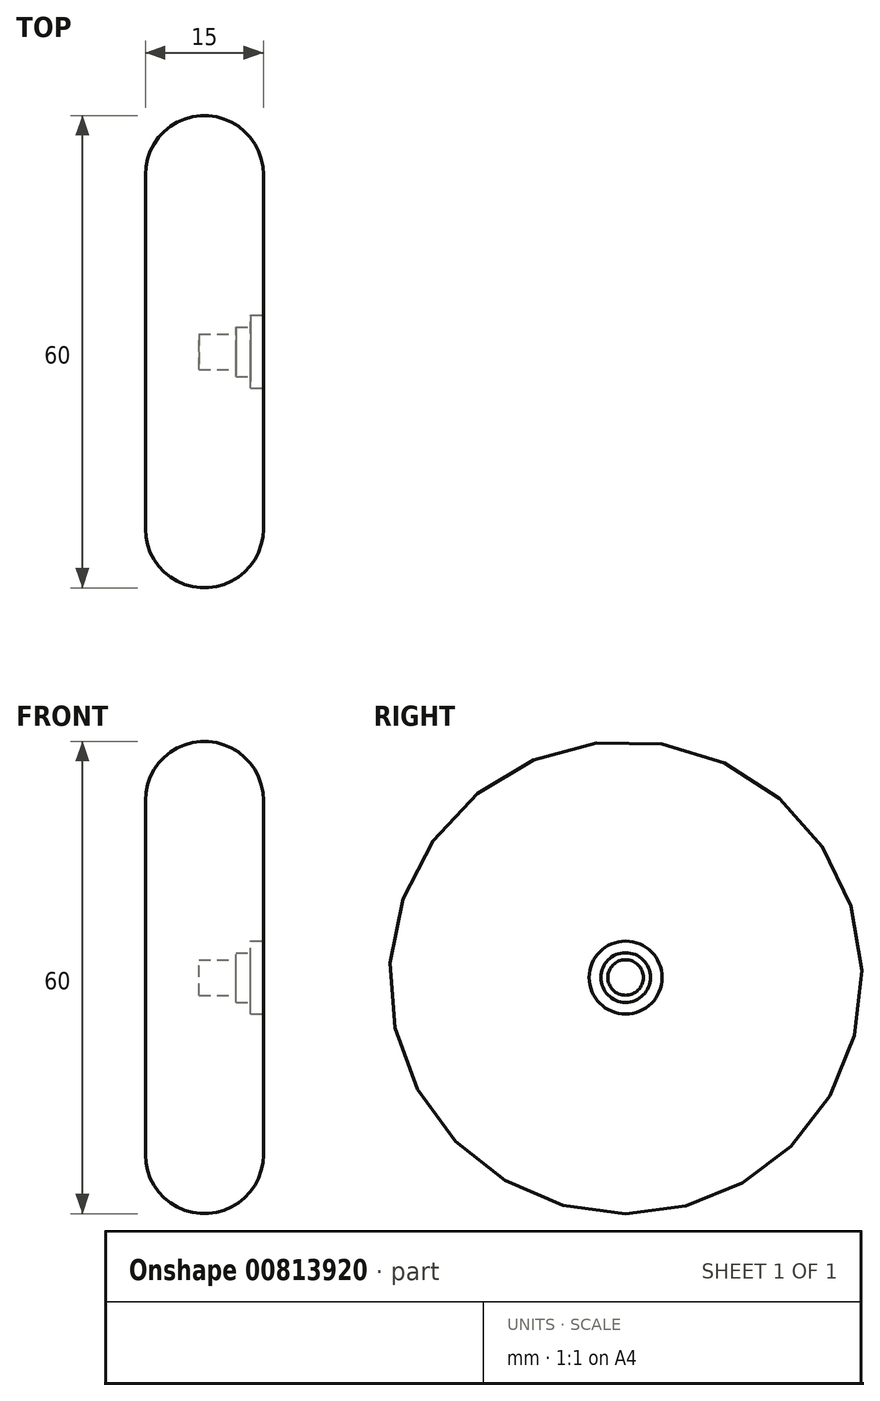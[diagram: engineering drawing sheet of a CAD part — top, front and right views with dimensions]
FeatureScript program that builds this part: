
annotation { "Feature Type Name" : "Feature", "Feature Type Description" : "" }
export const myFeature = defineFeature(function(context is Context, id is Id, definition is map)
    precondition{}
    {
        {
            var Q0;
            Q0=qCreatedBy(makeId("Front.planeOp"),FACE);
            var sketch = newSketch(context, id + "F0", { "sketchPlane" : qUnion([Q0])});
            skLineSegment(sketch, "E0", {"start": v(-10.33, 0) * mm, "end": v(-10.33, 22.5) * mm});
            skLineSegment(sketch, "E1", {"start": v(4.67, 22.5) * mm, "end": v(4.67, 4.63) * mm});
            skLineSegment(sketch, "E2", {"start": v(4.67, 4.63) * mm, "end": v(3.03, 4.63) * mm});
            skLineSegment(sketch, "E3", {"start": v(3.03, 4.63) * mm, "end": v(3.03, 3.15) * mm});
            skLineSegment(sketch, "E4", {"start": v(3.03, 3.15) * mm, "end": v(1.18, 3.15) * mm});
            skLineSegment(sketch, "E5", {"start": v(1.18, 3.15) * mm, "end": v(1.18, 2.26) * mm});
            skLineSegment(sketch, "E6", {"start": v(1.18, 2.26) * mm, "end": v(-3.54, 2.26) * mm});
            skLineSegment(sketch, "E7", {"start": v(-3.54, 2.26) * mm, "end": v(-3.54, 0) * mm});
            skLineSegment(sketch, "E8", {"start": v(-3.54, 0) * mm, "end": v(-10.33, 0) * mm});
            skArc(sketch, "E9", {"start": v(4.67, 22.5) * mm, "mid": v(-2.83, 30) * mm, "end": v(-10.33, 22.5) * mm});
            skSolve(sketch);
        }
        {
            var Q0;
            Q0=makeQuery(id+"F0.imprint","IMPRINT",FACE,{"disambiguationData":[TD([[makeQuery(id+"F0.imprint","IMPRINT",EDGE,{"derivedFrom":sQuery(id+"F0.wireOp",EDGE,"E0")}),-1.0]])]});
            var Q1;
            Q1=sQuery(id+"F0.wireOp",EDGE,"E8");
            revolve(context, id + "F1", {"surfaceOperationType" : NewSurfaceOperationType.NEW, "entities" : qUnion([Q0]), "axis" : qUnion([Q1]), "revolveType" : RevolveType.FULL});
        }
    });
